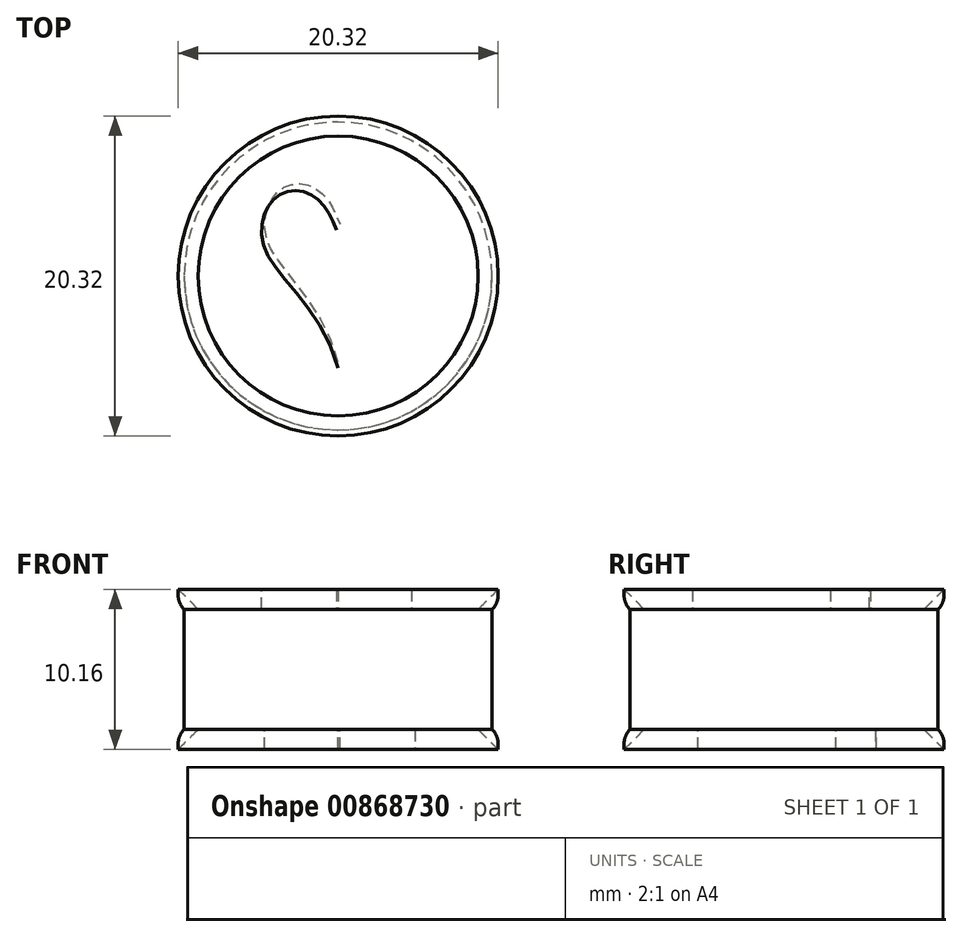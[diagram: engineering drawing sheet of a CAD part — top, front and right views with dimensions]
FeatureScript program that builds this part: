
annotation { "Feature Type Name" : "Feature", "Feature Type Description" : "" }
export const myFeature = defineFeature(function(context is Context, id is Id, definition is map)
    precondition{}
    {
        {
            var Q0;
            Q0=qCreatedBy(makeId("Top.planeOp"),FACE);
            var sketch = newSketch(context, id + "F0", { "sketchPlane" : qUnion([Q0])});
            skCircle(sketch, "E0", {"center": v(0, 0) * mm, "radius": 9.78 * mm});
            skSolve(sketch);
        }
        {
            var Q0;
            Q0 = qSketchRegion(id + "F0", true);
            extrude(context, id + "F1", {"entities" : qUnion([Q0]), "depth" : 7.62 * mm, "offsetDistance" : 25.4 * mm});
        }
        {
            var Q0;
            Q0=makeQuery(id+"F1.opExtrude","CAP_FACE",FACE,{"disambiguationData":[OSD([sQuery(id+"F0.wireOp",EDGE,"E0")])],"isStart":false});
            var sketch = newSketch(context, id + "F2", { "sketchPlane" : qUnion([Q0])});
            skCircle(sketch, "E1", {"center": v(0, 0) * mm, "radius": 8.9 * mm});
            skCircle(sketch, "E2", {"center": v(0, 0) * mm, "radius": 10.16 * mm});
            skSolve(sketch);
        }
        {
            var Q0;
            Q0 = qSketchRegion(id + "F2", true);
            extrude(context, id + "F3", {"entities" : qUnion([Q0]), "operationType" : NewBodyOperationType.ADD, "depth" : 2.54 * mm, "offsetDistance" : 25.4 * mm});
        }
        {
            var Q0;
            Q0=makeQuery(id+"F3.opExtrude","CAP_EDGE",EDGE,{"disambiguationData":[OSD([sQuery(id+"F2.wireOp",EDGE,"E1")])],"isStart":false});
            chamfer(context, id + "F4", {"entities" : qUnion([Q0]), "width" : 2.54 * mm, "tangentPropagation" : true});
        }
        {
            var Q0;
            Q0=makeQuery(id+"F1.opExtrude","CAP_FACE",FACE,{"disambiguationData":[OSD([sQuery(id+"F0.wireOp",EDGE,"E0")])],"isStart":true});
            var sketch = newSketch(context, id + "F5", { "sketchPlane" : qUnion([Q0])});
            skCircle(sketch, "E3", {"center": v(0, 0) * mm, "radius": 10.16 * mm});
            skCircle(sketch, "E4", {"center": v(0, 0) * mm, "radius": 8.9 * mm});
            skSolve(sketch);
        }
        {
            var Q0;
            Q0 = qSketchRegion(id + "F5", true);
            extrude(context, id + "F6", {"entities" : qUnion([Q0]), "operationType" : NewBodyOperationType.ADD, "depth" : 2.54 * mm, "offsetDistance" : 25.4 * mm});
        }
        {
            var Q0;
            Q0=makeQuery(id+"F6.opExtrude","CAP_EDGE",EDGE,{"disambiguationData":[OSD([sQuery(id+"F5.wireOp",EDGE,"E4")])],"isStart":false});
            chamfer(context, id + "F7", {"entities" : qUnion([Q0]), "width" : 2.54 * mm, "tangentPropagation" : true});
        }
        {
            var Q0;
            Q0=makeQuery(id+"F1.opExtrude","CAP_FACE",FACE,{"disambiguationData":[OSD([sQuery(id+"F0.wireOp",EDGE,"E0")])],"isStart":false});
            var sketch = newSketch(context, id + "F8", { "sketchPlane" : qUnion([Q0])});
            skFitSpline(sketch, "E5", {"points": [v(0, -5.83) * mm, v(-4.41, 1.2) * mm, v(-4.76, 3.68) * mm, v(-3.76, 5.14) * mm, v(-2.32, 5.39) * mm, v(-0.97, 4.56) * mm, v(-0.1, 2.93) * mm], "startDerivative": vector(-10.25, 35.96) * mm, "endDerivative": vector(5.16, -12.45) * mm});
            skLineSegment(sketch, "E6", {"start": v(0, -5.83) * mm, "end": v(-0.1, 2.93) * mm});
            skFitSpline(sketch, "E7.MirrorCS", {"points": [v(0, -5.83) * mm, v(4.24, 1.3) * mm, v(4.53, 3.8) * mm, v(3.5, 5.23) * mm, v(2.05, 5.44) * mm, v(0.73, 4.58) * mm, v(-0.1, 2.93) * mm], "startDerivative": vector(9.4, 36.2) * mm, "endDerivative": vector(-4.86, -12.57) * mm});
            skSolve(sketch);
        }
        {
            var Q0;
            Q0 = qSketchRegion(id + "F8", true);
            extrude(context, id + "F9", {"entities" : qUnion([Q0]), "operationType" : NewBodyOperationType.ADD, "depth" : 1.27 * mm, "offsetDistance" : 25.4 * mm});
        }
        {
            var Q0;
            Q0=makeQuery(id+"F1.opExtrude","CAP_FACE",FACE,{"disambiguationData":[OSD([sQuery(id+"F0.wireOp",EDGE,"E0")])],"isStart":true});
            var sketch = newSketch(context, id + "F10", { "sketchPlane" : qUnion([Q0])});
            skFitSpline(sketch, "E8", {"points": [v(0, 5.46) * mm, v(4.41, -1.57) * mm, v(4.76, -4.05) * mm, v(3.76, -5.51) * mm, v(2.32, -5.76) * mm, v(0.97, -4.92) * mm, v(0.1, -3.3) * mm], "startDerivative": vector(10.25, -35.96) * mm, "endDerivative": vector(-5.16, 12.45) * mm});
            skLineSegment(sketch, "E9", {"start": v(0, 5.46) * mm, "end": v(0.1, -3.3) * mm});
            skFitSpline(sketch, "E10.MirrorCS", {"points": [v(0, 5.46) * mm, v(-4.24, -1.68) * mm, v(-4.53, -4.16) * mm, v(-3.5, -5.6) * mm, v(-2.05, -5.81) * mm, v(-0.73, -4.94) * mm, v(0.1, -3.3) * mm], "startDerivative": vector(-9.4, -36.2) * mm, "endDerivative": vector(4.86, 12.57) * mm});
            skSolve(sketch);
        }
        {
            var Q0;
            Q0 = qSketchRegion(id + "F10", true);
            extrude(context, id + "F11", {"entities" : qUnion([Q0]), "operationType" : NewBodyOperationType.ADD, "depth" : 1.27 * mm, "offsetDistance" : 25.4 * mm});
        }
        {
            var Q0;
            Q0=makeQuery(id+"F6.opExtrude","CAP_EDGE",EDGE,{"disambiguationData":[OSD([sQuery(id+"F5.wireOp",EDGE,"E3")])],"isStart":true});
            var Q1;
            Q1=makeQuery(id+"F3.opExtrude","CAP_EDGE",EDGE,{"disambiguationData":[OSD([sQuery(id+"F2.wireOp",EDGE,"E2")])],"isStart":true});
            fillet(context, id + "F12", {"entities" : qUnion([Q0, Q1]), "radius" : 1.27 * mm, "tangentPropagation" : true, "allowEdgeOverflow" : false});
        }
    });
